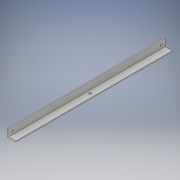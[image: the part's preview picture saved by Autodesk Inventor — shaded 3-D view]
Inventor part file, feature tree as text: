
AUTODESK INVENTOR PART (.ipt)
format: ipt  version: 2017 (Build 210142000, 142)  size: 119,808 bytes
history: native  units: in
note: dims shown in document units (in); Inventor stores cm internally (conversion verified against a paired STEP export)
features: hole x2, sketch x2, extrude x1
ambient origin geometry x8: Origin, YZ Plane, XZ Plane, XY Plane, X Axis, Y Axis, Z Axis, Center Point
bodies: Solid1 (feature_tree)
feature tree (5):
  extrude  "Extrusion1"  Depth=1.0in
  hole  "mount"  [1 undecoded]
  hole  "Hole5"  [1 undecoded]
  sketch  "Sketch7"  dims[d0=1.0in d1=1.0in]
  sketch  "Sketch8"  dims[d2=0.125in d3=19.375in d4=0.0in d43=0.5in d44=0.5in d45=0.7874in d47=18.375in d48=0.3937in d50=1.0in d52=0.266in d53=0.75in d54=0.507in d55=0.25in d56=0.5635in d57=1.0in d58=0.8108in d59=0.5in d60=0.266in d61=0.75in d62=0.507in d63=0.25in d64=0.5635in d65=1.0in d66=0.8108in]
note: 2 required parameter values undecoded (feature->parameter linkage not recoverable at this tier; creation-order binding heuristic only, values carry confidence <= 0.55)
